# Revit family: SIGNUM LP50 2m
name_source: partatom
category: HLS-Bauteile
units: mm (PartAtom-declared; Revit-internal decimal feet)

## family parameters
Arbeitsebenenbasiert = Ja
Beim Laden mit Abzugskörper schneiden = Nein
Bemaßung runder Anschluss = Durchmesser verwenden
Beschriftungsausrichtung beibehalten = Nein
Gemeinsam genutzt = Ja
Immer vertikal = Nein
Raumberechnungspunkt = Nein
Teiletyp = Normal

## types (1)
- SIGNUM LP50  L=2000
    Abmessung = 27/50/1.5 mm
    Artikelnummer = 0800201
    Breite = 27 mm  [stored 0.0885827 ft]
    Bund = 216 m
    EAN = 4250928467508
    Fabrikat = MEFA
    Firma = MEFA Befestigungs- und Montagesysteme GmbH
    Fläche (schwächster Profilquerschnitt) = 0 m²
    Gewicht = 1,11 kg
    Höhe = 50 mm
    Kurztext1 = SIGNUM LP50
    Kurztext2 = 27 / 50 / 1,5 mm L= 2 m fbv
    Langloch = 11.0 x 40.0 mm
    Länge = 2000 mm  [stored 6.56168 ft]
    Material = Stahl
    Materialname = S250
    Mengeneinheit = m
    Profil = SIGNUM
    Profiltyp = LP50
    Schlitzbreite = 11 mm
    Schwerpunktabstand eo = 2.5 cm
    Schwerpunktabstand eu = 2.5 cm
    Schwerpunktabstand ez = 1.54 cm
    Streckgrenze = 250 N/mm²
    Stärke = 2 mm  [stored 0.00656168 ft]
    Trägheitsradius iy = 1.97 cm
    Trägheitsradius iz = 1.37 cm
    Vorgabe-Ansicht = 1219 mm
    Widerstandsmoment Wy = 2.01 cm³
    Widerstandsmoment Wz = 0.87 cm³
    vpe = 36

note: [stored X ft] marks values corroborated as IEEE doubles in the binary element streams (Revit-internal decimal feet)
